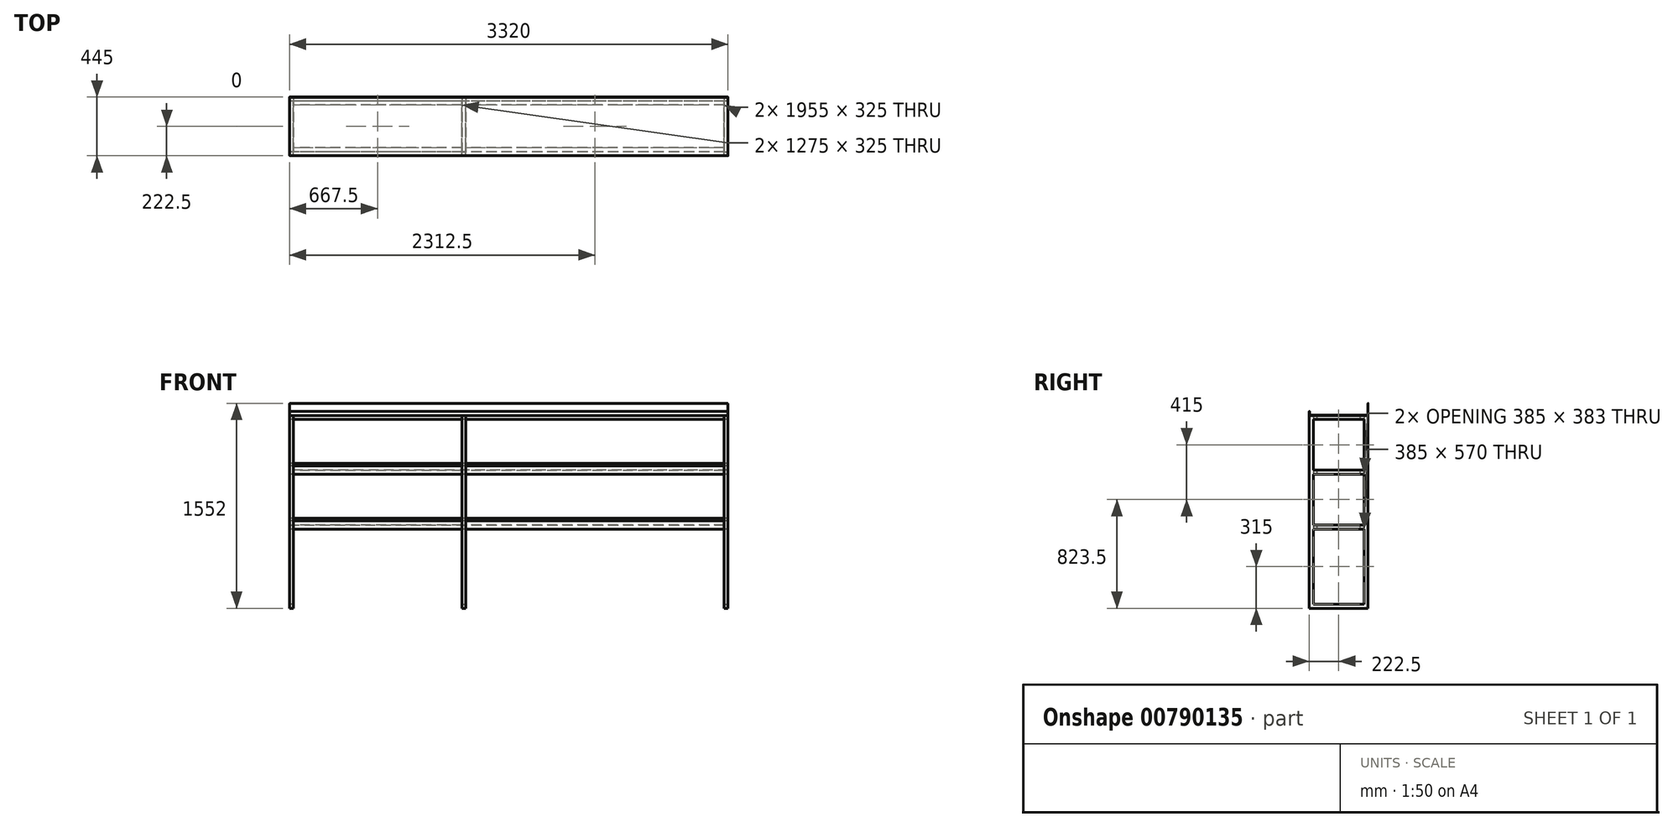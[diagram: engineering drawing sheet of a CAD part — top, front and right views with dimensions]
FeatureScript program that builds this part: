
annotation { "Feature Type Name" : "Feature", "Feature Type Description" : "" }
export const myFeature = defineFeature(function(context is Context, id is Id, definition is map)
    precondition{}
    {
        {
            var Q0;
            Q0=qCreatedBy(makeId("Top.planeOp"),FACE);
            var sketch = newSketch(context, id + "F0", { "sketchPlane" : qUnion([Q0])});
            skLineSegment(sketch, "E0.bottom", {"start": v(0, 0) * mm, "end": v(30, 0) * mm});
            skLineSegment(sketch, "E0.top", {"start": v(0, -30) * mm, "end": v(30, -30) * mm});
            skLineSegment(sketch, "E0.left", {"start": v(0, 0) * mm, "end": v(0, -30) * mm});
            skLineSegment(sketch, "E0.right", {"start": v(30, 0) * mm, "end": v(30, -30) * mm});
            skLineSegment(sketch, "E1.bottom", {"start": v(1305, 0) * mm, "end": v(1335, 0) * mm});
            skLineSegment(sketch, "E1.top", {"start": v(1305, -30) * mm, "end": v(1335, -30) * mm});
            skLineSegment(sketch, "E1.left", {"start": v(1305, 0) * mm, "end": v(1305, -30) * mm});
            skLineSegment(sketch, "E1.right", {"start": v(1335, 0) * mm, "end": v(1335, -30) * mm});
            skLineSegment(sketch, "E2.bottom", {"start": v(3290, 0) * mm, "end": v(3320, 0) * mm});
            skLineSegment(sketch, "E2.top", {"start": v(3290, -30) * mm, "end": v(3320, -30) * mm});
            skLineSegment(sketch, "E2.left", {"start": v(3290, 0) * mm, "end": v(3290, -30) * mm});
            skLineSegment(sketch, "E2.right", {"start": v(3320, 0) * mm, "end": v(3320, -30) * mm});
            skLineSegment(sketch, "E3.bottom", {"start": v(0, -445) * mm, "end": v(30, -445) * mm});
            skLineSegment(sketch, "E3.top", {"start": v(0, -415) * mm, "end": v(30, -415) * mm});
            skLineSegment(sketch, "E3.left", {"start": v(0, -445) * mm, "end": v(0, -415) * mm});
            skLineSegment(sketch, "E3.right", {"start": v(30, -445) * mm, "end": v(30, -415) * mm});
            skLineSegment(sketch, "E4.bottom", {"start": v(1335, -445) * mm, "end": v(1305, -445) * mm});
            skLineSegment(sketch, "E4.top", {"start": v(1335, -415) * mm, "end": v(1305, -415) * mm});
            skLineSegment(sketch, "E4.left", {"start": v(1335, -445) * mm, "end": v(1335, -415) * mm});
            skLineSegment(sketch, "E4.right", {"start": v(1305, -445) * mm, "end": v(1305, -415) * mm});
            skLineSegment(sketch, "E5.bottom", {"start": v(3320, -445) * mm, "end": v(3290, -445) * mm});
            skLineSegment(sketch, "E5.top", {"start": v(3320, -415) * mm, "end": v(3290, -415) * mm});
            skLineSegment(sketch, "E5.left", {"start": v(3320, -445) * mm, "end": v(3320, -415) * mm});
            skLineSegment(sketch, "E5.right", {"start": v(3290, -445) * mm, "end": v(3290, -415) * mm});
            skSolve(sketch);
        }
        {
            var Q0;
            Q0 = qSketchRegion(id + "F0", true);
            extrude(context, id + "F1", {"entities" : qUnion([Q0]), "depth" : 1460 * mm, "offsetDistance" : 25 * mm});
        }
        {
            var Q0;
            Q0=makeQuery(id+"F1.opExtrude","SWEPT_FACE",FACE,{"disambiguationData":[OSD([sQuery(id+"F0.wireOp",EDGE,"E0.left")])]});
            var sketch = newSketch(context, id + "F2", { "sketchPlane" : qUnion([Q0])});
            skLineSegment(sketch, "E6.bottom", {"start": v(30, 1460) * mm, "end": v(60, 1460) * mm});
            skLineSegment(sketch, "E6.top", {"start": v(30, 1430) * mm, "end": v(60, 1430) * mm});
            skLineSegment(sketch, "E6.left", {"start": v(30, 1460) * mm, "end": v(30, 1430) * mm});
            skLineSegment(sketch, "E6.right", {"start": v(60, 1460) * mm, "end": v(60, 1430) * mm});
            skLineSegment(sketch, "E7.bottom", {"start": v(415, 1460) * mm, "end": v(385, 1460) * mm});
            skLineSegment(sketch, "E7.top", {"start": v(415, 1430) * mm, "end": v(385, 1430) * mm});
            skLineSegment(sketch, "E7.left", {"start": v(415, 1460) * mm, "end": v(415, 1430) * mm});
            skLineSegment(sketch, "E7.right", {"start": v(385, 1460) * mm, "end": v(385, 1430) * mm});
            skLineSegment(sketch, "E8.bottom", {"start": v(30, 1045) * mm, "end": v(60, 1045) * mm});
            skLineSegment(sketch, "E8.top", {"start": v(30, 1015) * mm, "end": v(60, 1015) * mm});
            skLineSegment(sketch, "E8.left", {"start": v(30, 1045) * mm, "end": v(30, 1015) * mm});
            skLineSegment(sketch, "E8.right", {"start": v(60, 1045) * mm, "end": v(60, 1015) * mm});
            skLineSegment(sketch, "E9.bottom", {"start": v(385, 1045) * mm, "end": v(415, 1045) * mm});
            skLineSegment(sketch, "E9.top", {"start": v(385, 1015) * mm, "end": v(415, 1015) * mm});
            skLineSegment(sketch, "E9.left", {"start": v(385, 1045) * mm, "end": v(385, 1015) * mm});
            skLineSegment(sketch, "E9.right", {"start": v(415, 1045) * mm, "end": v(415, 1015) * mm});
            skLineSegment(sketch, "E10.bottom", {"start": v(30, 630) * mm, "end": v(60, 630) * mm});
            skLineSegment(sketch, "E10.top", {"start": v(30, 600) * mm, "end": v(60, 600) * mm});
            skLineSegment(sketch, "E10.left", {"start": v(30, 630) * mm, "end": v(30, 600) * mm});
            skLineSegment(sketch, "E10.right", {"start": v(60, 630) * mm, "end": v(60, 600) * mm});
            skLineSegment(sketch, "E11.bottom", {"start": v(385, 630) * mm, "end": v(415, 630) * mm});
            skLineSegment(sketch, "E11.top", {"start": v(385, 600) * mm, "end": v(415, 600) * mm});
            skLineSegment(sketch, "E11.left", {"start": v(385, 630) * mm, "end": v(385, 600) * mm});
            skLineSegment(sketch, "E11.right", {"start": v(415, 630) * mm, "end": v(415, 600) * mm});
            skSolve(sketch);
        }
        {
            var Q0;
            Q0 = qSketchRegion(id + "F2", true);
            extrude(context, id + "F3", {"entities" : qUnion([Q0]), "operationType" : NewBodyOperationType.ADD, "oppositeDirection" : true, "depth" : 3320 * mm, "offsetDistance" : 25 * mm});
        }
        {
            var Q0;
            Q0=makeQuery(id+"F3.opExtrude","SWEPT_FACE",FACE,{"disambiguationData":[OSD([sQuery(id+"F2.wireOp",EDGE,"E6.right")])]});
            var sketch = newSketch(context, id + "F4", { "sketchPlane" : qUnion([Q0])});
            skLineSegment(sketch, "E12.bottom", {"start": v(0, 1460) * mm, "end": v(30, 1460) * mm});
            skLineSegment(sketch, "E12.top", {"start": v(0, 1430) * mm, "end": v(30, 1430) * mm});
            skLineSegment(sketch, "E12.left", {"start": v(0, 1460) * mm, "end": v(0, 1430) * mm});
            skLineSegment(sketch, "E12.right", {"start": v(30, 1460) * mm, "end": v(30, 1430) * mm});
            skLineSegment(sketch, "E13.bottom", {"start": v(1305, 1460) * mm, "end": v(1335, 1460) * mm});
            skLineSegment(sketch, "E13.top", {"start": v(1305, 1430) * mm, "end": v(1335, 1430) * mm});
            skLineSegment(sketch, "E13.left", {"start": v(1305, 1460) * mm, "end": v(1305, 1430) * mm});
            skLineSegment(sketch, "E13.right", {"start": v(1335, 1460) * mm, "end": v(1335, 1430) * mm});
            skLineSegment(sketch, "E14.bottom", {"start": v(3320, 1460) * mm, "end": v(3290, 1460) * mm});
            skLineSegment(sketch, "E14.top", {"start": v(3320, 1430) * mm, "end": v(3290, 1430) * mm});
            skLineSegment(sketch, "E14.left", {"start": v(3320, 1460) * mm, "end": v(3320, 1430) * mm});
            skLineSegment(sketch, "E14.right", {"start": v(3290, 1460) * mm, "end": v(3290, 1430) * mm});
            skLineSegment(sketch, "E15.0.1.0", {"start": v(30, 1045) * mm, "end": v(30, 1015) * mm});
            skLineSegment(sketch, "E15.0.1.1", {"start": v(0, 1045) * mm, "end": v(0, 1015) * mm});
            skLineSegment(sketch, "E15.0.1.2", {"start": v(0, 1015) * mm, "end": v(30, 1015) * mm});
            skLineSegment(sketch, "E15.0.1.3", {"start": v(0, 1045) * mm, "end": v(30, 1045) * mm});
            skLineSegment(sketch, "E15.0.1.4", {"start": v(3290, 1045) * mm, "end": v(3290, 1015) * mm});
            skLineSegment(sketch, "E15.0.1.5", {"start": v(3320, 1045) * mm, "end": v(3320, 1015) * mm});
            skLineSegment(sketch, "E15.0.1.6", {"start": v(3320, 1015) * mm, "end": v(3290, 1015) * mm});
            skLineSegment(sketch, "E15.0.1.7", {"start": v(3320, 1045) * mm, "end": v(3290, 1045) * mm});
            skLineSegment(sketch, "E15.0.1.8", {"start": v(1305, 1045) * mm, "end": v(1305, 1015) * mm});
            skLineSegment(sketch, "E15.0.1.9", {"start": v(1305, 1015) * mm, "end": v(1335, 1015) * mm});
            skLineSegment(sketch, "E15.0.1.10", {"start": v(1305, 1045) * mm, "end": v(1335, 1045) * mm});
            skLineSegment(sketch, "E15.0.1.11", {"start": v(1335, 1045) * mm, "end": v(1335, 1015) * mm});
            skLineSegment(sketch, "E15.0.2.0", {"start": v(30, 630) * mm, "end": v(30, 600) * mm});
            skLineSegment(sketch, "E15.0.2.1", {"start": v(0, 630) * mm, "end": v(0, 600) * mm});
            skLineSegment(sketch, "E15.0.2.2", {"start": v(0, 600) * mm, "end": v(30, 600) * mm});
            skLineSegment(sketch, "E15.0.2.3", {"start": v(0, 630) * mm, "end": v(30, 630) * mm});
            skLineSegment(sketch, "E15.0.2.4", {"start": v(3290, 630) * mm, "end": v(3290, 600) * mm});
            skLineSegment(sketch, "E15.0.2.5", {"start": v(3320, 630) * mm, "end": v(3320, 600) * mm});
            skLineSegment(sketch, "E15.0.2.6", {"start": v(3320, 600) * mm, "end": v(3290, 600) * mm});
            skLineSegment(sketch, "E15.0.2.7", {"start": v(3320, 630) * mm, "end": v(3290, 630) * mm});
            skLineSegment(sketch, "E15.0.2.8", {"start": v(1305, 630) * mm, "end": v(1305, 600) * mm});
            skLineSegment(sketch, "E15.0.2.9", {"start": v(1305, 600) * mm, "end": v(1335, 600) * mm});
            skLineSegment(sketch, "E15.0.2.10", {"start": v(1305, 630) * mm, "end": v(1335, 630) * mm});
            skLineSegment(sketch, "E15.0.2.11", {"start": v(1335, 630) * mm, "end": v(1335, 600) * mm});
            skLineSegment(sketch, "E15.direction1", {"start": v(0, 1430) * mm, "end": v(25, 1430) * mm, "construction": true});
            skLineSegment(sketch, "E15.direction2", {"start": v(0, 1430) * mm, "end": v(0, 1015) * mm, "construction": true});
            skSolve(sketch);
        }
        {
            var Q0;
            Q0 = qSketchRegion(id + "F4", true);
            extrude(context, id + "F5", {"entities" : qUnion([Q0]), "operationType" : NewBodyOperationType.ADD, "endBound" : BoundingType.UP_TO_NEXT, "depth" : 25 * mm, "offsetDistance" : 25 * mm});
        }
        {
            var Q0;
            Q0=makeQuery(id+"F5.boolean.opBoolean","MERGE",FACE,{"derivedFrom":[makeQuery(id+"F3.boolean.opBoolean","MERGE",FACE,{"derivedFrom":[makeQuery(id+"F1.opExtrude","CAP_FACE",FACE,{"disambiguationData":[OSD([sQuery(id+"F0.wireOp",EDGE,"E0.bottom"),sQuery(id+"F0.wireOp",EDGE,"E0.top"),sQuery(id+"F0.wireOp",EDGE,"E0.left"),sQuery(id+"F0.wireOp",EDGE,"E0.right")])],"isStart":false}),makeQuery(id+"F1.opExtrude","CAP_FACE",FACE,{"disambiguationData":[OSD([sQuery(id+"F0.wireOp",EDGE,"E1.bottom"),sQuery(id+"F0.wireOp",EDGE,"E1.top"),sQuery(id+"F0.wireOp",EDGE,"E1.left"),sQuery(id+"F0.wireOp",EDGE,"E1.right")])],"isStart":false}),makeQuery(id+"F1.opExtrude","CAP_FACE",FACE,{"disambiguationData":[OSD([sQuery(id+"F0.wireOp",EDGE,"E2.bottom"),sQuery(id+"F0.wireOp",EDGE,"E2.top"),sQuery(id+"F0.wireOp",EDGE,"E2.left"),sQuery(id+"F0.wireOp",EDGE,"E2.right")])],"isStart":false}),makeQuery(id+"F3.opExtrude","SWEPT_FACE",FACE,{"disambiguationData":[OSD([sQuery(id+"F2.wireOp",EDGE,"E6.bottom")])]})]}),makeQuery(id+"F3.boolean.opBoolean","MERGE",FACE,{"derivedFrom":[makeQuery(id+"F1.opExtrude","CAP_FACE",FACE,{"disambiguationData":[OSD([sQuery(id+"F0.wireOp",EDGE,"E3.bottom"),sQuery(id+"F0.wireOp",EDGE,"E3.top"),sQuery(id+"F0.wireOp",EDGE,"E3.left"),sQuery(id+"F0.wireOp",EDGE,"E3.right")])],"isStart":false}),makeQuery(id+"F1.opExtrude","CAP_FACE",FACE,{"disambiguationData":[OSD([sQuery(id+"F0.wireOp",EDGE,"E4.bottom"),sQuery(id+"F0.wireOp",EDGE,"E4.top"),sQuery(id+"F0.wireOp",EDGE,"E4.left"),sQuery(id+"F0.wireOp",EDGE,"E4.right")])],"isStart":false}),makeQuery(id+"F1.opExtrude","CAP_FACE",FACE,{"disambiguationData":[OSD([sQuery(id+"F0.wireOp",EDGE,"E5.bottom"),sQuery(id+"F0.wireOp",EDGE,"E5.top"),sQuery(id+"F0.wireOp",EDGE,"E5.left"),sQuery(id+"F0.wireOp",EDGE,"E5.right")])],"isStart":false}),makeQuery(id+"F3.opExtrude","SWEPT_FACE",FACE,{"disambiguationData":[OSD([sQuery(id+"F2.wireOp",EDGE,"E7.bottom")])]})]}),makeQuery(id+"F5.opExtrude","SWEPT_FACE",FACE,{"disambiguationData":[OSD([sQuery(id+"F4.wireOp",EDGE,"E12.bottom")])]}),makeQuery(id+"F5.opExtrude","SWEPT_FACE",FACE,{"disambiguationData":[OSD([sQuery(id+"F4.wireOp",EDGE,"E13.bottom")])]}),makeQuery(id+"F5.opExtrude","SWEPT_FACE",FACE,{"disambiguationData":[OSD([sQuery(id+"F4.wireOp",EDGE,"E14.bottom")])]})]});
            var sketch = newSketch(context, id + "F6", { "sketchPlane" : qUnion([Q0])});
            skLineSegment(sketch, "E16.bottom", {"start": v(0, 0) * mm, "end": v(3320, 0) * mm});
            skLineSegment(sketch, "E16.top", {"start": v(0, -445) * mm, "end": v(3320, -445) * mm});
            skLineSegment(sketch, "E16.left", {"start": v(0, 0) * mm, "end": v(0, -445) * mm});
            skLineSegment(sketch, "E16.right", {"start": v(3320, 0) * mm, "end": v(3320, -445) * mm});
            skSolve(sketch);
        }
        {
            var Q0;
            Q0 = qSketchRegion(id + "F6", true);
            extrude(context, id + "F7", {"entities" : qUnion([Q0]), "depth" : 2 * mm, "offsetDistance" : 25 * mm});
        }
        {
            var Q0;
            Q0=makeQuery(id+"F7.opExtrude","CAP_FACE",FACE,{"disambiguationData":[OSD([sQuery(id+"F6.wireOp",EDGE,"E16.bottom"),sQuery(id+"F6.wireOp",EDGE,"E16.top"),sQuery(id+"F6.wireOp",EDGE,"E16.left"),sQuery(id+"F6.wireOp",EDGE,"E16.right")])],"isStart":false});
            var sketch = newSketch(context, id + "F8", { "sketchPlane" : qUnion([Q0])});
            skLineSegment(sketch, "E17.bottom", {"start": v(3320, 0) * mm, "end": v(0, 0) * mm});
            skLineSegment(sketch, "E17.top", {"start": v(3320, -2) * mm, "end": v(0, -2) * mm});
            skLineSegment(sketch, "E17.left", {"start": v(3320, 0) * mm, "end": v(3320, -2) * mm});
            skLineSegment(sketch, "E17.right", {"start": v(0, 0) * mm, "end": v(0, -2) * mm});
            skLineSegment(sketch, "E18.bottom", {"start": v(3320, -445) * mm, "end": v(0, -445) * mm});
            skLineSegment(sketch, "E18.top", {"start": v(3320, -443) * mm, "end": v(0, -443) * mm});
            skLineSegment(sketch, "E18.left", {"start": v(3320, -445) * mm, "end": v(3320, -443) * mm});
            skLineSegment(sketch, "E18.right", {"start": v(0, -445) * mm, "end": v(0, -443) * mm});
            skSolve(sketch);
        }
        {
            var Q0;
            Q0=makeQuery(id+"F8.imprint","IMPRINT",FACE,{"disambiguationData":[TD([[makeQuery(id+"F8.imprint","IMPRINT",EDGE,{"derivedFrom":sQuery(id+"F8.wireOp",EDGE,"E18.bottom")}),1.0]])]});
            extrude(context, id + "F9", {"entities" : qUnion([Q0]), "operationType" : NewBodyOperationType.ADD, "depth" : 30 * mm, "offsetDistance" : 25 * mm});
        }
        {
            var Q0;
            Q0=makeQuery(id+"F8.imprint","IMPRINT",FACE,{"disambiguationData":[TD([[makeQuery(id+"F8.imprint","IMPRINT",EDGE,{"derivedFrom":sQuery(id+"F8.wireOp",EDGE,"E17.bottom")}),-1.0]])]});
            extrude(context, id + "F10", {"entities" : qUnion([Q0]), "operationType" : NewBodyOperationType.ADD, "depth" : 90 * mm, "offsetDistance" : 25 * mm});
        }
        {
            var Q0;
            Q0=makeQuery(id+"F5.boolean.opBoolean","MERGE",FACE,{"derivedFrom":[makeQuery(id+"F3.opExtrude","SWEPT_FACE",FACE,{"disambiguationData":[OSD([sQuery(id+"F2.wireOp",EDGE,"E8.bottom")])]}),makeQuery(id+"F3.opExtrude","SWEPT_FACE",FACE,{"disambiguationData":[OSD([sQuery(id+"F2.wireOp",EDGE,"E9.bottom")])]}),makeQuery(id+"F5.opExtrude","SWEPT_FACE",FACE,{"disambiguationData":[OSD([sQuery(id+"F4.wireOp",EDGE,"E15.0.1.3")])]}),makeQuery(id+"F5.opExtrude","SWEPT_FACE",FACE,{"disambiguationData":[OSD([sQuery(id+"F4.wireOp",EDGE,"E15.0.1.7")])]}),makeQuery(id+"F5.opExtrude","SWEPT_FACE",FACE,{"disambiguationData":[OSD([sQuery(id+"F4.wireOp",EDGE,"E15.0.1.10")])]})]});
            var sketch = newSketch(context, id + "F11", { "sketchPlane" : qUnion([Q0])});
            skLineSegment(sketch, "E19.bottom", {"start": v(0, -30) * mm, "end": v(3320, -30) * mm});
            skLineSegment(sketch, "E19.top", {"start": v(0, -415) * mm, "end": v(3320, -415) * mm});
            skLineSegment(sketch, "E19.left", {"start": v(0, -30) * mm, "end": v(0, -415) * mm});
            skLineSegment(sketch, "E19.right", {"start": v(3320, -30) * mm, "end": v(3320, -415) * mm});
            skSolve(sketch);
        }
        {
            var Q0;
            Q0 = qSketchRegion(id + "F11", true);
            extrude(context, id + "F12", {"entities" : qUnion([Q0]), "depth" : 2 * mm, "offsetDistance" : 25 * mm});
        }
        {
            var Q0;
            Q0=makeQuery(id+"F5.boolean.opBoolean","MERGE",FACE,{"derivedFrom":[makeQuery(id+"F3.opExtrude","SWEPT_FACE",FACE,{"disambiguationData":[OSD([sQuery(id+"F2.wireOp",EDGE,"E10.bottom")])]}),makeQuery(id+"F3.opExtrude","SWEPT_FACE",FACE,{"disambiguationData":[OSD([sQuery(id+"F2.wireOp",EDGE,"E11.bottom")])]}),makeQuery(id+"F5.opExtrude","SWEPT_FACE",FACE,{"disambiguationData":[OSD([sQuery(id+"F4.wireOp",EDGE,"E15.0.2.3")])]}),makeQuery(id+"F5.opExtrude","SWEPT_FACE",FACE,{"disambiguationData":[OSD([sQuery(id+"F4.wireOp",EDGE,"E15.0.2.7")])]}),makeQuery(id+"F5.opExtrude","SWEPT_FACE",FACE,{"disambiguationData":[OSD([sQuery(id+"F4.wireOp",EDGE,"E15.0.2.10")])]})]});
            var sketch = newSketch(context, id + "F13", { "sketchPlane" : qUnion([Q0])});
            skLineSegment(sketch, "E20.bottom", {"start": v(0, -30) * mm, "end": v(3320, -30) * mm});
            skLineSegment(sketch, "E20.top", {"start": v(0, -415) * mm, "end": v(3320, -415) * mm});
            skLineSegment(sketch, "E20.left", {"start": v(0, -30) * mm, "end": v(0, -415) * mm});
            skLineSegment(sketch, "E20.right", {"start": v(3320, -30) * mm, "end": v(3320, -415) * mm});
            skSolve(sketch);
        }
        {
            var Q0;
            Q0 = qSketchRegion(id + "F13", true);
            extrude(context, id + "F14", {"entities" : qUnion([Q0]), "depth" : 2 * mm, "offsetDistance" : 25 * mm});
        }
        {
            var Q0;
            Q0=makeQuery(id+"F12.opExtrude","CAP_FACE",FACE,{"disambiguationData":[OSD([sQuery(id+"F11.wireOp",EDGE,"E19.bottom"),sQuery(id+"F11.wireOp",EDGE,"E19.top"),sQuery(id+"F11.wireOp",EDGE,"E19.left"),sQuery(id+"F11.wireOp",EDGE,"E19.right")])],"isStart":false});
            var sketch = newSketch(context, id + "F15", { "sketchPlane" : qUnion([Q0])});
            skLineSegment(sketch, "E21.bottom", {"start": v(3320, -30) * mm, "end": v(0, -30) * mm});
            skLineSegment(sketch, "E21.top", {"start": v(3320, -32) * mm, "end": v(0, -32) * mm});
            skLineSegment(sketch, "E21.left", {"start": v(3320, -30) * mm, "end": v(3320, -32) * mm});
            skLineSegment(sketch, "E21.right", {"start": v(0, -30) * mm, "end": v(0, -32) * mm});
            skLineSegment(sketch, "E22.bottom", {"start": v(0, -415) * mm, "end": v(3320, -415) * mm});
            skLineSegment(sketch, "E22.top", {"start": v(0, -413) * mm, "end": v(3320, -413) * mm});
            skLineSegment(sketch, "E22.left", {"start": v(0, -415) * mm, "end": v(0, -413) * mm});
            skLineSegment(sketch, "E22.right", {"start": v(3320, -415) * mm, "end": v(3320, -413) * mm});
            skSolve(sketch);
        }
        {
            var Q0;
            Q0=makeQuery(id+"F15.imprint","IMPRINT",FACE,{"disambiguationData":[TD([[makeQuery(id+"F15.imprint","IMPRINT",EDGE,{"derivedFrom":sQuery(id+"F15.wireOp",EDGE,"E22.bottom")}),-1.0]])]});
            extrude(context, id + "F16", {"entities" : qUnion([Q0]), "operationType" : NewBodyOperationType.ADD, "depth" : 30 * mm, "offsetDistance" : 25 * mm});
        }
        {
            var Q0;
            Q0=makeQuery(id+"F14.opExtrude","CAP_FACE",FACE,{"disambiguationData":[OSD([sQuery(id+"F13.wireOp",EDGE,"E20.bottom"),sQuery(id+"F13.wireOp",EDGE,"E20.top"),sQuery(id+"F13.wireOp",EDGE,"E20.left"),sQuery(id+"F13.wireOp",EDGE,"E20.right")])],"isStart":false});
            var sketch = newSketch(context, id + "F17", { "sketchPlane" : qUnion([Q0])});
            skLineSegment(sketch, "E23.bottom", {"start": v(0, -30) * mm, "end": v(3320, -30) * mm});
            skLineSegment(sketch, "E23.top", {"start": v(0, -32) * mm, "end": v(3320, -32) * mm});
            skLineSegment(sketch, "E23.left", {"start": v(0, -30) * mm, "end": v(0, -32) * mm});
            skLineSegment(sketch, "E23.right", {"start": v(3320, -30) * mm, "end": v(3320, -32) * mm});
            skLineSegment(sketch, "E24.bottom", {"start": v(0, -415) * mm, "end": v(3320, -415) * mm});
            skLineSegment(sketch, "E24.top", {"start": v(0, -413) * mm, "end": v(3320, -413) * mm});
            skLineSegment(sketch, "E24.left", {"start": v(0, -415) * mm, "end": v(0, -413) * mm});
            skLineSegment(sketch, "E24.right", {"start": v(3320, -415) * mm, "end": v(3320, -413) * mm});
            skSolve(sketch);
        }
        {
            var Q0;
            Q0=makeQuery(id+"F17.imprint","IMPRINT",FACE,{"disambiguationData":[TD([[makeQuery(id+"F17.imprint","IMPRINT",EDGE,{"derivedFrom":sQuery(id+"F17.wireOp",EDGE,"E24.bottom")}),-1.0]])]});
            extrude(context, id + "F18", {"entities" : qUnion([Q0]), "operationType" : NewBodyOperationType.ADD, "depth" : 30 * mm, "offsetDistance" : 25 * mm});
        }
        {
            var Q0;
            Q0=makeQuery(id+"F9.opExtrude","CAP_EDGE",EDGE,{"disambiguationData":[OSD([sQuery(id+"F8.wireOp",EDGE,"E18.right")])],"isStart":false});
            var Q1;
            Q1=makeQuery(id+"F9.opExtrude","CAP_EDGE",EDGE,{"disambiguationData":[OSD([sQuery(id+"F8.wireOp",EDGE,"E18.left")])],"isStart":false});
            var Q2;
            Q2=makeQuery(id+"F10.opExtrude","CAP_EDGE",EDGE,{"disambiguationData":[OSD([sQuery(id+"F8.wireOp",EDGE,"E17.left")])],"isStart":false});
            var Q3;
            Q3=makeQuery(id+"F10.opExtrude","CAP_EDGE",EDGE,{"disambiguationData":[OSD([sQuery(id+"F8.wireOp",EDGE,"E17.right")])],"isStart":false});
            fillet(context, id + "F19", {"entities" : qUnion([Q0, Q1, Q2, Q3]), "radius" : 5 * mm, "tangentPropagation" : true, "allowEdgeOverflow" : false});
        }
        {
            var Q0;
            {var subQ3=sQuery(id+"F2.wireOp",EDGE,"E10.top");var subQ4=sQuery(id+"F0.wireOp",EDGE,"E0.top");Q0=makeQuery(id+"F3.boolean.opBoolean","SPLIT",FACE,{"disambiguationData":[TD([makeQuery(id+"F3.opExtrude","SWEPT_FACE",FACE,{"disambiguationData":[OSD([subQ3])]})])],"derivedFrom":makeQuery(id+"F1.opExtrude","SWEPT_FACE",FACE,{"disambiguationData":[OSD([subQ4])]})});}
            var sketch = newSketch(context, id + "F20", { "sketchPlane" : qUnion([Q0])});
            skLineSegment(sketch, "E25.bottom", {"start": v(0, 0) * mm, "end": v(30, 0) * mm});
            skLineSegment(sketch, "E25.top", {"start": v(0, 30) * mm, "end": v(30, 30) * mm});
            skLineSegment(sketch, "E25.left", {"start": v(0, 0) * mm, "end": v(0, 30) * mm});
            skLineSegment(sketch, "E25.right", {"start": v(30, 0) * mm, "end": v(30, 30) * mm});
            skLineSegment(sketch, "E26.bottom", {"start": v(1305, 0) * mm, "end": v(1335, 0) * mm});
            skLineSegment(sketch, "E26.top", {"start": v(1305, 30) * mm, "end": v(1335, 30) * mm});
            skLineSegment(sketch, "E26.left", {"start": v(1305, 0) * mm, "end": v(1305, 30) * mm});
            skLineSegment(sketch, "E26.right", {"start": v(1335, 0) * mm, "end": v(1335, 30) * mm});
            skLineSegment(sketch, "E27.bottom", {"start": v(3290, 0) * mm, "end": v(3320, 0) * mm});
            skLineSegment(sketch, "E27.top", {"start": v(3290, 30) * mm, "end": v(3320, 30) * mm});
            skLineSegment(sketch, "E27.left", {"start": v(3290, 0) * mm, "end": v(3290, 30) * mm});
            skLineSegment(sketch, "E27.right", {"start": v(3320, 0) * mm, "end": v(3320, 30) * mm});
            skSolve(sketch);
        }
        {
            var Q0;
            Q0 = qSketchRegion(id + "F20", true);
            extrude(context, id + "F21", {"entities" : qUnion([Q0]), "operationType" : NewBodyOperationType.ADD, "endBound" : BoundingType.UP_TO_NEXT, "depth" : 25 * mm, "offsetDistance" : 25 * mm});
        }
        {
            var Q0;
            Q0=makeQuery(id+"F15.imprint","IMPRINT",FACE,{"disambiguationData":[TD([[makeQuery(id+"F15.imprint","IMPRINT",EDGE,{"derivedFrom":sQuery(id+"F15.wireOp",EDGE,"E21.bottom")}),1.0]])]});
            extrude(context, id + "F22", {"entities" : qUnion([Q0]), "operationType" : NewBodyOperationType.ADD, "depth" : 50 * mm, "offsetDistance" : 25 * mm});
        }
        {
            var Q0;
            Q0=makeQuery(id+"F17.imprint","IMPRINT",FACE,{"disambiguationData":[TD([[makeQuery(id+"F17.imprint","IMPRINT",EDGE,{"derivedFrom":sQuery(id+"F17.wireOp",EDGE,"E23.bottom")}),1.0]])]});
            extrude(context, id + "F23", {"entities" : qUnion([Q0]), "operationType" : NewBodyOperationType.ADD, "depth" : 50 * mm, "offsetDistance" : 25 * mm});
        }
    });
